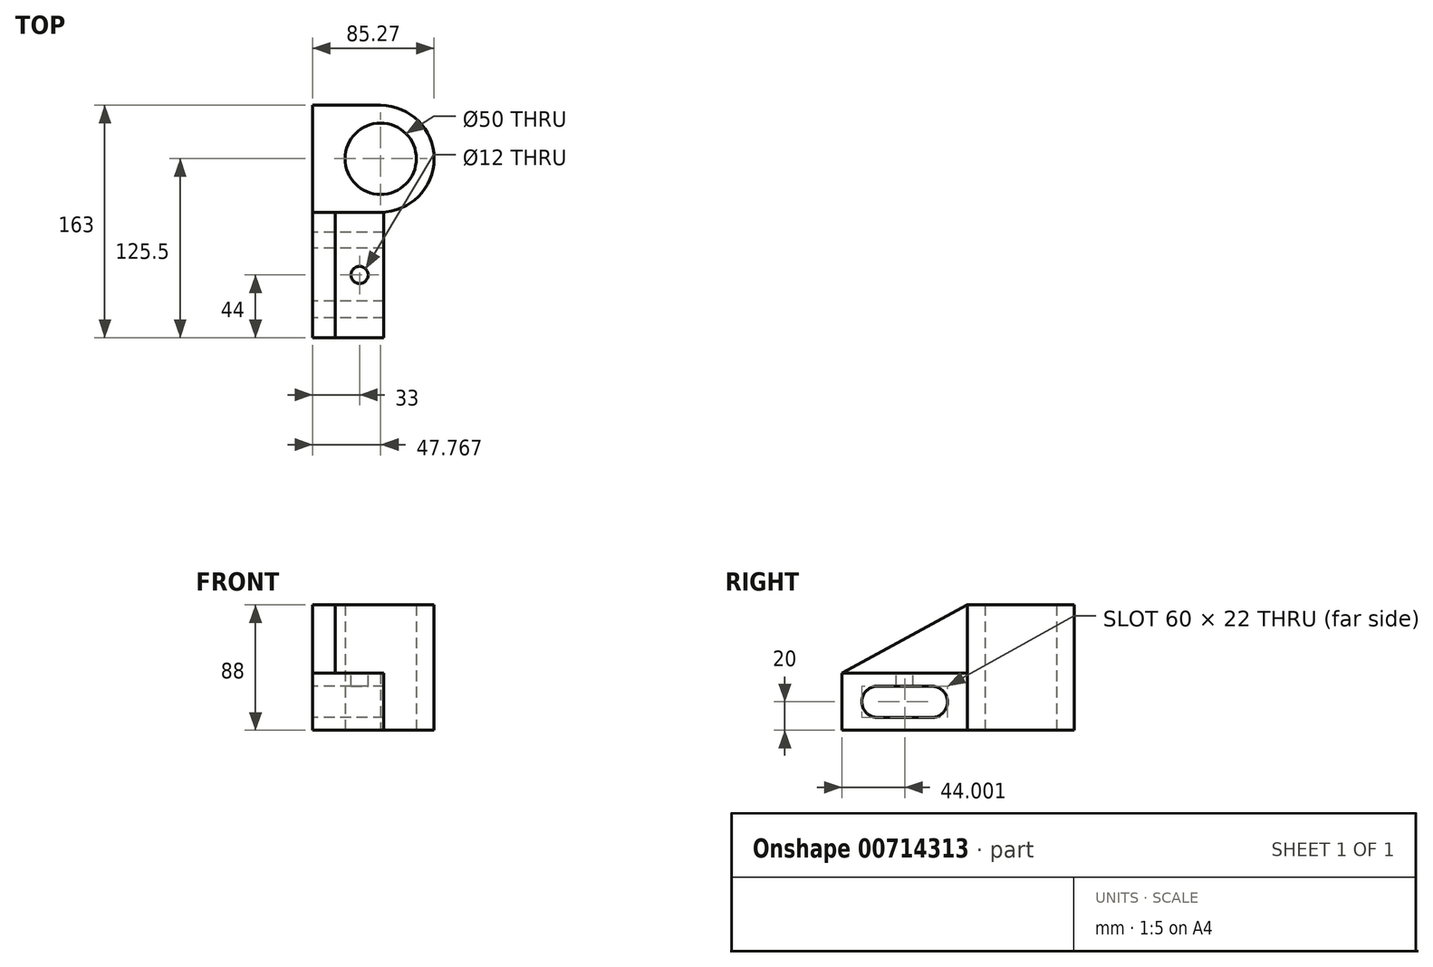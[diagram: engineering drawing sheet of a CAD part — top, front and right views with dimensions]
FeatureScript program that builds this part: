
annotation { "Feature Type Name" : "Feature", "Feature Type Description" : "" }
export const myFeature = defineFeature(function(context is Context, id is Id, definition is map)
    precondition{}
    {
        {
            var Q0;
            Q0=qCreatedBy(makeId("Top.planeOp"),FACE);
            var sketch = newSketch(context, id + "F0", { "sketchPlane" : qUnion([Q0])});
            skLineSegment(sketch, "E0", {"start": v(0, 0) * mm, "end": v(47.77, 0) * mm});
            skLineSegment(sketch, "E1", {"start": v(47.77, 75) * mm, "end": v(0, 75) * mm});
            skLineSegment(sketch, "E2", {"start": v(0, 75) * mm, "end": v(0, 0) * mm});
            skCircle(sketch, "E3", {"center": v(47.77, 37.5) * mm, "radius": 25 * mm});
            skArc(sketch, "E4", {"start": v(47.77, 0) * mm, "mid": v(85.27, 37.5) * mm, "end": v(47.77, 75) * mm});
            skPoint(sketch, "E5.end.orphan", {"position": v(0, 59) * mm});
            skSolve(sketch);
        }
        {
            var Q0;
            Q0 = qSketchRegion(id + "F0", true);
            extrude(context, id + "F1", {"entities" : qUnion([Q0]), "depth" : 88 * mm, "offsetDistance" : 25 * mm});
        }
        {
            var Q0;
            Q0=qCreatedBy(makeId("Right.planeOp"),FACE);
            var sketch = newSketch(context, id + "F2", { "sketchPlane" : qUnion([Q0])});
            skLineSegment(sketch, "E6.bottom", {"start": v(0, 0) * mm, "end": v(-88, 0) * mm});
            skLineSegment(sketch, "E6.top", {"start": v(0, 40) * mm, "end": v(-88, 40) * mm});
            skLineSegment(sketch, "E6.left", {"start": v(0, 0) * mm, "end": v(0, 40) * mm});
            skLineSegment(sketch, "E6.right", {"start": v(-88, 0) * mm, "end": v(-88, 40) * mm});
            skArc(sketch, "E7", {"start": v(-62.51, 30.99) * mm, "mid": v(-74, 20.24) * mm, "end": v(-63, 9) * mm});
            skArc(sketch, "E8", {"start": v(-25.35, 9) * mm, "mid": v(-14, 19.83) * mm, "end": v(-25, 31) * mm});
            skLineSegment(sketch, "E9", {"start": v(-63.5, 30.99) * mm, "end": v(-25, 31) * mm});
            skLineSegment(sketch, "E10", {"start": v(-25.35, 9) * mm, "end": v(-63, 9) * mm});
            skSolve(sketch);
        }
        {
            var Q0;
            Q0 = qSketchRegion(id + "F2", true);
            extrude(context, id + "F3", {"entities" : qUnion([Q0]), "operationType" : NewBodyOperationType.ADD, "depth" : 50 * mm, "offsetDistance" : 25 * mm});
        }
        {
            var Q0;
            Q0=qCreatedBy(makeId("Right.planeOp"),FACE);
            var sketch = newSketch(context, id + "F4", { "sketchPlane" : qUnion([Q0])});
            skLineSegment(sketch, "E11", {"start": v(0, 40) * mm, "end": v(0, 88) * mm});
            skLineSegment(sketch, "E12", {"start": v(0, 88) * mm, "end": v(-88, 40) * mm});
            skLineSegment(sketch, "E13", {"start": v(-88, 40) * mm, "end": v(0, 40) * mm});
            skSolve(sketch);
        }
        {
            var Q0;
            Q0=makeQuery(id+"F4.imprint","IMPRINT",FACE,{"disambiguationData":[TD([[makeQuery(id+"F4.imprint","IMPRINT",EDGE,{"derivedFrom":sQuery(id+"F4.wireOp",EDGE,"E11")}),1.0]])]});
            extrude(context, id + "F5", {"entities" : qUnion([Q0]), "operationType" : NewBodyOperationType.ADD, "depth" : 16 * mm, "offsetDistance" : 25 * mm});
        }
        {
            var Q0;
            Q0=makeQuery(id+"F3.opExtrude","SWEPT_FACE",FACE,{"disambiguationData":[OSD([sQuery(id+"F2.wireOp",EDGE,"E6.top")])]});
            var sketch = newSketch(context, id + "F6", { "sketchPlane" : qUnion([Q0])});
            skLineSegment(sketch, "E14", {"start": v(0, 0) * mm, "end": v(33, 0) * mm});
            skLineSegment(sketch, "E15", {"start": v(33, 0) * mm, "end": v(33, -44) * mm});
            skCircle(sketch, "E16", {"center": v(33, -44) * mm, "radius": 6 * mm});
            skSolve(sketch);
        }
        {
            var Q0;
            Q0=makeQuery(id+"F6.imprint","IMPRINT",FACE,{"disambiguationData":[TD([[makeQuery(id+"F6.imprint","IMPRINT",EDGE,{"derivedFrom":sQuery(id+"F6.wireOp",EDGE,"E16")}),1.0]])]});
            extrude(context, id + "F7", {"entities" : qUnion([Q0]), "operationType" : NewBodyOperationType.REMOVE, "endBound" : BoundingType.UP_TO_NEXT, "oppositeDirection" : true, "depth" : 25 * mm, "offsetDistance" : 25 * mm});
        }
    });
